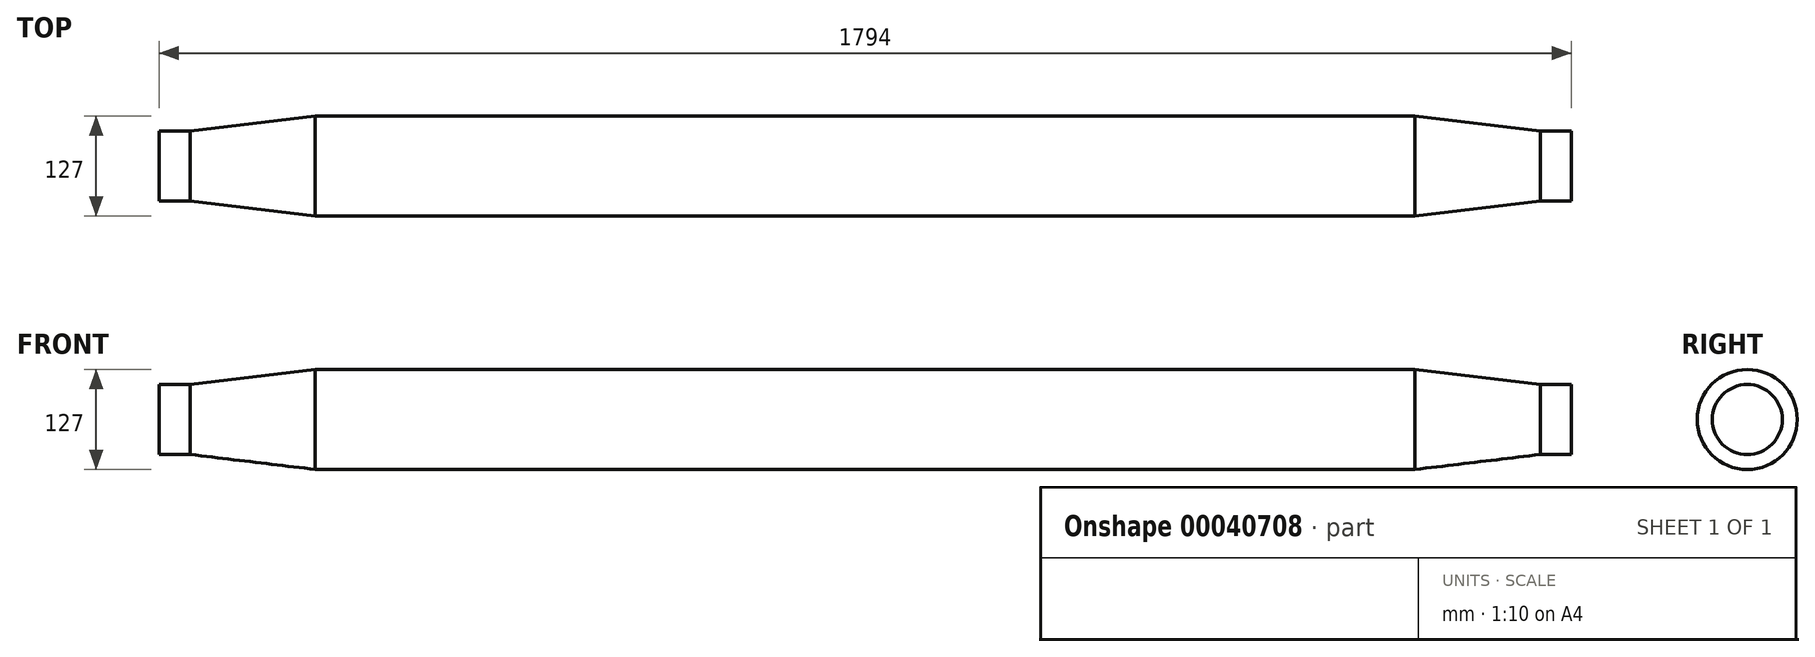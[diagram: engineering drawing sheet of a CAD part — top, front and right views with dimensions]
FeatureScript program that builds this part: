
annotation { "Feature Type Name" : "Feature", "Feature Type Description" : "" }
export const myFeature = defineFeature(function(context is Context, id is Id, definition is map)
    precondition{}
    {
        {
            var Q0;
            Q0=qCreatedBy(makeId("Right.planeOp"),FACE);
            var sketch = newSketch(context, id + "F0", { "sketchPlane" : qUnion([Q0])});
            skCircle(sketch, "E0", {"center": v(0, 0) * mm, "radius": 63.5 * mm});
            skSolve(sketch);
        }
        {
            var Q0;
            Q0 = qSketchRegion(id + "F0", true);
            extrude(context, id + "F1", {"entities" : qUnion([Q0]), "endBound" : BoundingType.SYMMETRIC, "depth" : 1397 * mm});
        }
        {
            var Q0;
            Q0=qCreatedBy(makeId("Right.planeOp"),FACE);
            cPlane(context, id + "F2", {"entities" : qUnion([Q0]), "cplaneType" : CPlaneType.OFFSET, "offset" : 897 * mm, "width" : 152.4 * mm, "height" : 152.4 * mm});
        }
        {
            var Q0;
            Q0=qCreatedBy(id+"F2.planeOp",FACE);
            var sketch = newSketch(context, id + "F3", { "sketchPlane" : qUnion([Q0])});
            skCircle(sketch, "E1", {"center": v(0, 0) * mm, "radius": 44.45 * mm});
            skSolve(sketch);
        }
        {
            var Q0;
            Q0 = qSketchRegion(id + "F3", true);
            extrude(context, id + "F4", {"entities" : qUnion([Q0]), "oppositeDirection" : true, "depth" : 39.62 * mm});
        }
        {
            var Q0;
            Q0=makeQuery(id+"F4.opExtrude","CAP_FACE",FACE,{"disambiguationData":[OSD([sQuery(id+"F3.wireOp",EDGE,"E1")])],"isStart":false});
            var Q1;
            Q1=makeQuery(id+"F1.opExtrude","CAP_FACE",FACE,{"disambiguationData":[OSD([sQuery(id+"F0.wireOp",EDGE,"E0")])],"isStart":false});
            loft(context, id + "F5", {"sheetProfilesArray" : [{ "sheetProfileEntities" : qUnion([Q0]) }, { "sheetProfileEntities" : qUnion([Q1]) }]});
        }
        {
            var Q0;
            Q0=makeQuery(id+"F5.opLoft","SWEPT_BODY",BODY,{"disambiguationData":[OSD([sQuery(id+"F0.wireOp",EDGE,"E0"),sQuery(id+"F3.wireOp",EDGE,"E1")])]});
            var Q1;
            Q1=makeQuery(id+"F4.opExtrude","SWEPT_BODY",BODY,{"disambiguationData":[OSD([sQuery(id+"F3.wireOp",EDGE,"E1")])]});
            var Q2;
            Q2=qCreatedBy(makeId("Right.planeOp"),FACE);
            mirror(context, id + "F6", {"operationType" : NewBodyOperationType.ADD, "entities" : qUnion([Q0, Q1]), "mirrorPlane" : qUnion([Q2])});
        }
    });
